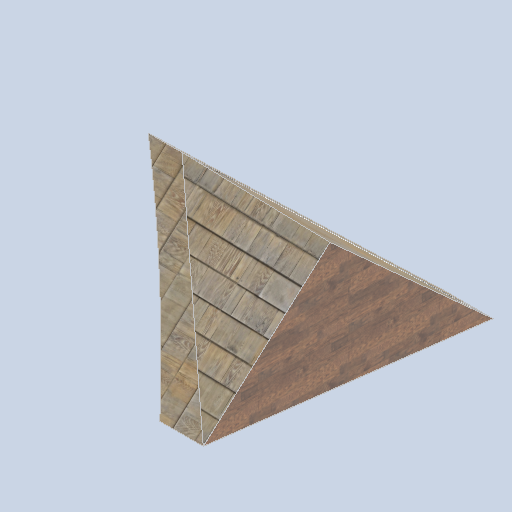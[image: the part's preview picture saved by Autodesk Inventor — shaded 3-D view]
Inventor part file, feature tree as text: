
AUTODESK INVENTOR PART (.ipt)
format: ipt  version: 2024.2 (Build 282272000, 272)  size: 284,672 bytes
history: native  units: in
note: dims shown in document units (in); Inventor stores cm internally (conversion verified against a paired STEP export)
features: sketch x7, plane x6, other x3
ambient origin geometry x8: Origin, YZ Plane, XZ Plane, XY Plane, X Axis, Y Axis, Z Axis, Center Point
bodies: Solid1 (feature_tree)
feature tree (16):
  other  "panel_pad_02 .ipt"
  other  "Solid1::panel_pad_02 .ipt"
  other  "TaggingFeature1"
  sketch  "Sketch1"  dims[d0=0.3937in]
  sketch  "Sketch2"
  sketch  "Sketch3"
  sketch  "Sketch6"
  sketch  "Sketch7"
  sketch  "Sketch8"
  sketch  "Sketch9"
  plane  "Work Plane1"
  plane  "Work Plane2"
  plane  "Work Plane3"
  plane  "Work Plane4"
  plane  "Work Plane5"
  plane  "Work Plane6"
